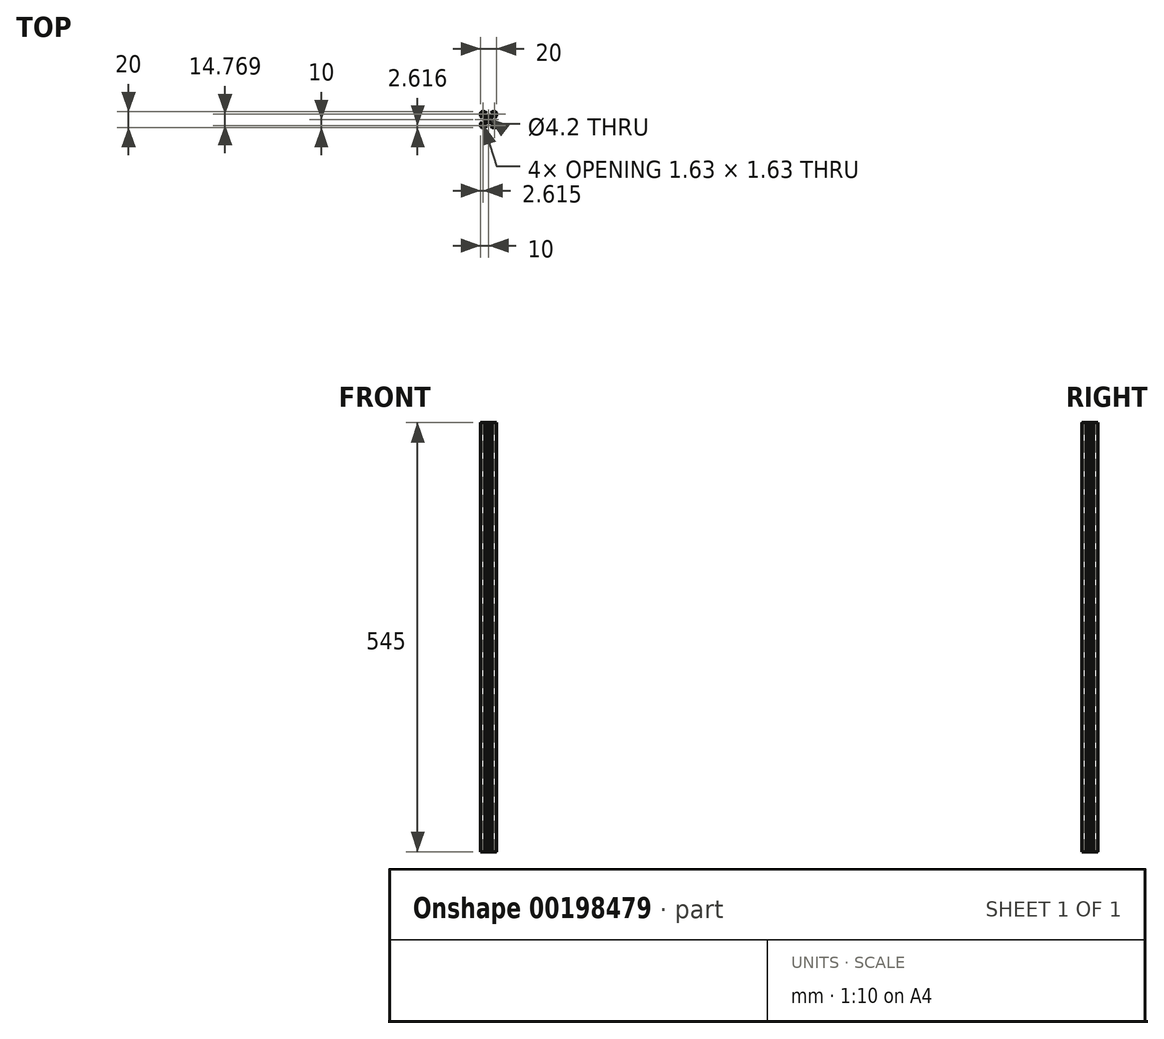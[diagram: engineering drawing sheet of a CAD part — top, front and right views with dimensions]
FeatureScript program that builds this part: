
annotation { "Feature Type Name" : "Feature", "Feature Type Description" : "" }
export const myFeature = defineFeature(function(context is Context, id is Id, definition is map)
    precondition{}
    {
        {
            var Q0;
            Q0=qCreatedBy(makeId("Top.planeOp"),FACE);
            var sketch = newSketch(context, id + "F0", { "sketchPlane" : qUnion([Q0])});
            skLineSegment(sketch, "E0", {"start": v(10, 8.27) * mm, "end": v(10, 4.41) * mm});
            skLineSegment(sketch, "E1", {"start": v(8.5, -10.23) * mm, "end": v(4.64, -10.23) * mm});
            skLineSegment(sketch, "E2", {"start": v(-10, -8.73) * mm, "end": v(-10, -4.87) * mm});
            skLineSegment(sketch, "E3", {"start": v(-8.5, 9.77) * mm, "end": v(-4.64, 9.77) * mm});
            skLineSegment(sketch, "E4.0", {"start": v(-5.5, 7.97) * mm, "end": v(-2.84, 7.97) * mm});
            skLineSegment(sketch, "E4.1", {"start": v(-8.2, -5.73) * mm, "end": v(-8.2, -3.07) * mm});
            skLineSegment(sketch, "E4.2", {"start": v(5.5, -8.43) * mm, "end": v(2.84, -8.43) * mm});
            skLineSegment(sketch, "E4.3", {"start": v(8.2, 5.27) * mm, "end": v(8.2, 2.61) * mm});
            skLineSegment(sketch, "E5.trimOffspring", {"start": v(4.64, 9.77) * mm, "end": v(8.5, 9.77) * mm});
            skPoint(sketch, "E6.start.orphan", {"position": v(0, 9.77) * mm});
            skLineSegment(sketch, "E7", {"start": v(-2.84, 7.97) * mm, "end": v(-4.64, 9.77) * mm});
            skLineSegment(sketch, "E8.trimOffspring", {"start": v(2.84, 7.97) * mm, "end": v(5.5, 7.97) * mm});
            skLineSegment(sketch, "E9.MirrorCS", {"start": v(2.84, 7.97) * mm, "end": v(4.64, 9.77) * mm});
            skLineSegment(sketch, "E10.MirrorCS", {"start": v(2.84, -8.43) * mm, "end": v(4.64, -10.23) * mm});
            skLineSegment(sketch, "E11.MirrorCS", {"start": v(-2.84, -8.43) * mm, "end": v(-4.64, -10.23) * mm});
            skLineSegment(sketch, "E12.trimOffspring", {"start": v(-2.84, -8.43) * mm, "end": v(-5.5, -8.43) * mm});
            skLineSegment(sketch, "E13.trimOffspring", {"start": v(-4.64, -10.23) * mm, "end": v(-8.5, -10.23) * mm});
            skLineSegment(sketch, "E14", {"start": v(-8.2, 2.61) * mm, "end": v(-10, 4.41) * mm});
            skLineSegment(sketch, "E15", {"start": v(-8.2, -3.07) * mm, "end": v(-10, -4.87) * mm});
            skLineSegment(sketch, "E16.trimOffspring", {"start": v(-10, 4.41) * mm, "end": v(-10, 8.27) * mm});
            skLineSegment(sketch, "E17.trimOffspring", {"start": v(-8.2, 2.61) * mm, "end": v(-8.2, 5.27) * mm});
            skLineSegment(sketch, "E18.MirrorCS", {"start": v(8.2, 2.61) * mm, "end": v(10, 4.41) * mm});
            skLineSegment(sketch, "E19.MirrorCS", {"start": v(8.2, -3.07) * mm, "end": v(10, -4.87) * mm});
            skLineSegment(sketch, "E20.trimOffspring", {"start": v(8.2, -3.07) * mm, "end": v(8.2, -5.73) * mm});
            skLineSegment(sketch, "E21.trimOffspring", {"start": v(10, -4.87) * mm, "end": v(10, -8.73) * mm});
            skCircle(sketch, "E22", {"center": v(0, -0.23) * mm, "radius": 2.1 * mm});
            skLineSegment(sketch, "E23", {"start": v(-6.56, 5.27) * mm, "end": v(-3.9, 2.61) * mm});
            skLineSegment(sketch, "E24", {"start": v(-5.5, 6.33) * mm, "end": v(-2.84, 3.67) * mm});
            skLineSegment(sketch, "E25", {"start": v(-5.5, 6.33) * mm, "end": v(-5.5, 7.97) * mm});
            skLineSegment(sketch, "E26", {"start": v(-6.56, 5.27) * mm, "end": v(-8.2, 5.27) * mm});
            skLineSegment(sketch, "E27", {"start": v(6.56, 5.27) * mm, "end": v(3.9, 2.61) * mm});
            skLineSegment(sketch, "E28", {"start": v(5.5, 6.33) * mm, "end": v(2.84, 3.67) * mm});
            skLineSegment(sketch, "E29", {"start": v(-6.56, -5.73) * mm, "end": v(-8.2, -5.73) * mm});
            skLineSegment(sketch, "E30", {"start": v(-5.5, -6.79) * mm, "end": v(-5.5, -8.43) * mm});
            skLineSegment(sketch, "E31", {"start": v(5.5, 6.33) * mm, "end": v(5.5, 7.97) * mm});
            skLineSegment(sketch, "E32", {"start": v(6.56, 5.27) * mm, "end": v(8.2, 5.27) * mm});
            skLineSegment(sketch, "E33", {"start": v(5.5, -6.79) * mm, "end": v(5.5, -8.43) * mm});
            skLineSegment(sketch, "E34", {"start": v(6.56, -5.73) * mm, "end": v(8.2, -5.73) * mm});
            skLineSegment(sketch, "E35.trimOffspring", {"start": v(2.84, -4.13) * mm, "end": v(5.5, -6.79) * mm});
            skLineSegment(sketch, "E36.trimOffspring", {"start": v(-2.84, -4.13) * mm, "end": v(-5.5, -6.79) * mm});
            skLineSegment(sketch, "E37.trimOffspring", {"start": v(-3.9, -3.07) * mm, "end": v(-6.56, -5.73) * mm});
            skLineSegment(sketch, "E38.trimOffspring", {"start": v(3.9, -3.07) * mm, "end": v(6.56, -5.73) * mm});
            skLineSegment(sketch, "E39", {"start": v(-3.9, -3.07) * mm, "end": v(-3.9, -0.48) * mm});
            skLineSegment(sketch, "E40", {"start": v(-2.84, 3.67) * mm, "end": v(-0.25, 3.67) * mm});
            skLineSegment(sketch, "E41", {"start": v(-2.84, -4.13) * mm, "end": v(-0.25, -4.13) * mm});
            skLineSegment(sketch, "E42", {"start": v(3.9, 2.61) * mm, "end": v(3.9, 0.02) * mm});
            skLineSegment(sketch, "E43", {"start": v(-8.2, 6.34) * mm, "end": v(-8.2, 7.97) * mm});
            skLineSegment(sketch, "E44", {"start": v(-6.57, 7.97) * mm, "end": v(-8.2, 7.97) * mm});
            skLineSegment(sketch, "E45", {"start": v(-8.2, 6.34) * mm, "end": v(-7.63, 6.34) * mm});
            skLineSegment(sketch, "E46", {"start": v(-6.57, 7.97) * mm, "end": v(-6.57, 7.4) * mm});
            skLineSegment(sketch, "E47", {"start": v(-7.63, 6.34) * mm, "end": v(-6.57, 7.4) * mm});
            skLineSegment(sketch, "E48.MirrorCS", {"start": v(6.57, 7.97) * mm, "end": v(8.2, 7.97) * mm});
            skLineSegment(sketch, "E49.MirrorCS", {"start": v(8.2, 6.34) * mm, "end": v(8.2, 7.97) * mm});
            skLineSegment(sketch, "E50.MirrorCS", {"start": v(8.2, 6.34) * mm, "end": v(7.63, 6.34) * mm});
            skLineSegment(sketch, "E51.MirrorCS", {"start": v(7.63, 6.34) * mm, "end": v(6.57, 7.4) * mm});
            skLineSegment(sketch, "E52.MirrorCS", {"start": v(6.57, 7.97) * mm, "end": v(6.57, 7.4) * mm});
            skLineSegment(sketch, "E53.MirrorCS", {"start": v(6.57, -8.43) * mm, "end": v(6.57, -7.86) * mm});
            skLineSegment(sketch, "E54.MirrorCS", {"start": v(8.2, -6.8) * mm, "end": v(7.63, -6.8) * mm});
            skLineSegment(sketch, "E55.MirrorCS", {"start": v(7.63, -6.8) * mm, "end": v(6.57, -7.86) * mm});
            skLineSegment(sketch, "E56.MirrorCS", {"start": v(6.57, -8.43) * mm, "end": v(8.2, -8.43) * mm});
            skLineSegment(sketch, "E57.MirrorCS", {"start": v(8.2, -6.8) * mm, "end": v(8.2, -8.43) * mm});
            skLineSegment(sketch, "E58.MirrorCS", {"start": v(-6.57, -8.43) * mm, "end": v(-8.2, -8.43) * mm});
            skLineSegment(sketch, "E59.MirrorCS", {"start": v(-8.2, -6.8) * mm, "end": v(-7.63, -6.8) * mm});
            skLineSegment(sketch, "E60.MirrorCS", {"start": v(-8.2, -6.8) * mm, "end": v(-8.2, -8.43) * mm});
            skLineSegment(sketch, "E61.MirrorCS", {"start": v(-7.63, -6.8) * mm, "end": v(-6.57, -7.86) * mm});
            skLineSegment(sketch, "E62.MirrorCS", {"start": v(-6.57, -8.43) * mm, "end": v(-6.57, -7.86) * mm});
            skPoint(sketch, "E63.visualSharp", {"position": v(-10, 9.77) * mm});
            skArc(sketch, "E63.filletArc", {"start": v(-8.5, 9.77) * mm, "mid": v(-9.56, 9.33) * mm, "end": v(-10, 8.27) * mm});
            skPoint(sketch, "E64.visualSharp", {"position": v(10, 9.77) * mm});
            skArc(sketch, "E64.filletArc", {"start": v(10, 8.27) * mm, "mid": v(9.56, 9.33) * mm, "end": v(8.5, 9.77) * mm});
            skPoint(sketch, "E65.visualSharp", {"position": v(10, -10.23) * mm});
            skArc(sketch, "E65.filletArc", {"start": v(8.5, -10.23) * mm, "mid": v(9.56, -9.8) * mm, "end": v(10, -8.73) * mm});
            skPoint(sketch, "E66.visualSharp", {"position": v(-10, -10.23) * mm});
            skArc(sketch, "E66.filletArc", {"start": v(-10, -8.73) * mm, "mid": v(-9.56, -9.8) * mm, "end": v(-8.5, -10.23) * mm});
            skLineSegment(sketch, "E67", {"start": v(-3.65, -0.23) * mm, "end": v(-3.9, 0.02) * mm});
            skLineSegment(sketch, "E68.MirrorCS", {"start": v(-3.65, -0.23) * mm, "end": v(-3.9, -0.48) * mm});
            skLineSegment(sketch, "E69.trimOffspring", {"start": v(-3.9, 0.02) * mm, "end": v(-3.9, 2.61) * mm});
            skLineSegment(sketch, "E70.MirrorCS", {"start": v(3.65, -0.23) * mm, "end": v(3.9, 0.02) * mm});
            skLineSegment(sketch, "E71.MirrorCS", {"start": v(3.65, -0.23) * mm, "end": v(3.9, -0.48) * mm});
            skLineSegment(sketch, "E72", {"start": v(0, -3.88) * mm, "end": v(0.25, -4.13) * mm});
            skLineSegment(sketch, "E73.MirrorCS", {"start": v(0, -3.88) * mm, "end": v(-0.25, -4.13) * mm});
            skLineSegment(sketch, "E74.trimOffspring", {"start": v(0.25, -4.13) * mm, "end": v(2.84, -4.13) * mm});
            skLineSegment(sketch, "E75.trimOffspring", {"start": v(3.9, -0.48) * mm, "end": v(3.9, -3.07) * mm});
            skLineSegment(sketch, "E76.MirrorCS", {"start": v(0, 3.42) * mm, "end": v(-0.25, 3.67) * mm});
            skLineSegment(sketch, "E77.MirrorCS", {"start": v(0, 3.42) * mm, "end": v(0.25, 3.67) * mm});
            skLineSegment(sketch, "E78.trimOffspring", {"start": v(0.25, 3.67) * mm, "end": v(2.84, 3.67) * mm});
            skSolve(sketch);
        }
        {
            var Q0;
            Q0 = qSketchRegion(id + "F0", true);
            extrude(context, id + "F1", {"entities" : qUnion([Q0]), "depth" : (505 + 40) * mm});
        }
    });
